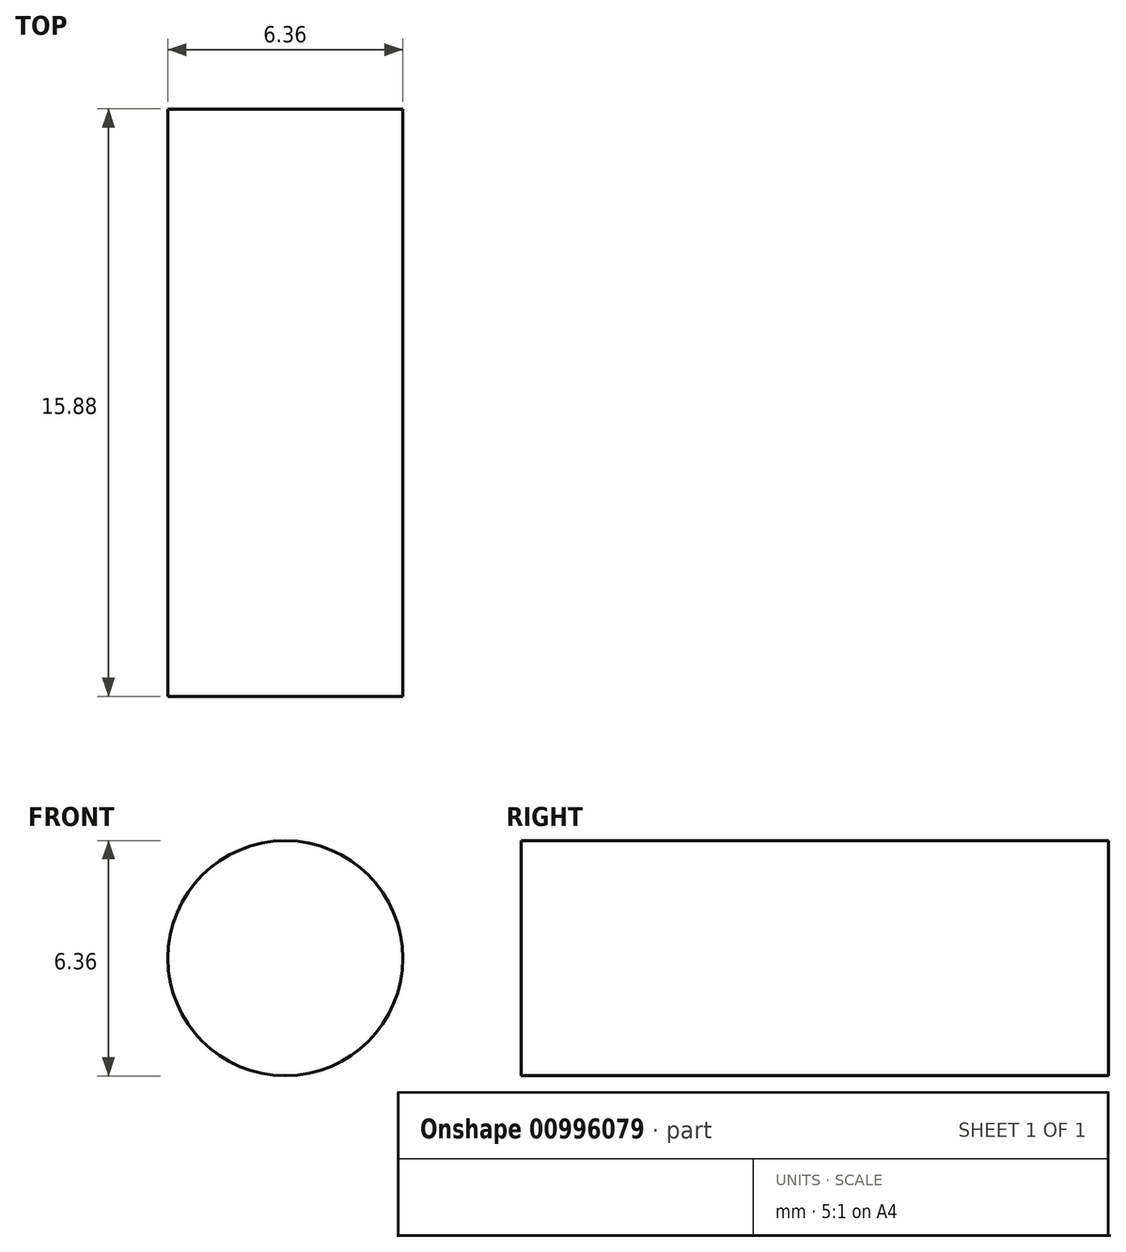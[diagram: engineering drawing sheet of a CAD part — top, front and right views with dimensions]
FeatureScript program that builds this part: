
annotation { "Feature Type Name" : "Feature", "Feature Type Description" : "" }
export const myFeature = defineFeature(function(context is Context, id is Id, definition is map)
    precondition{}
    {
        {
            var Q0;
            Q0=qCreatedBy(makeId("Front.planeOp"), FACE);
            var sketch = newSketch(context, id + "F0", { "sketchPlane" : qUnion([Q0])});
            skCircle(sketch, "E0.0", {"center": v(0, 0) * mm, "radius": 3.17 * mm});
            skSolve(sketch);
        }
        {
            var Q0;
            Q0 = qSketchRegion(id + "F0", true);
            extrude(context, id + "F1", {"entities" : qUnion([Q0]), "flatOperationType" : FlatOperationType.REMOVE, "oppositeDirection" : true, "depth" : 15.88 * mm, "offsetDistance" : 25.4 * mm, "domain" : OperationDomain.MODEL});
        }
    });
